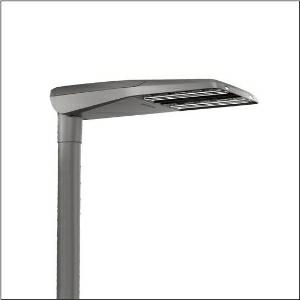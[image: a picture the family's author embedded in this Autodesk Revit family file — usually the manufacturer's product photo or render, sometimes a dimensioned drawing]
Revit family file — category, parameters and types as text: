
# Revit family: streetlight_sl_11_iq_midi___st1_0p1_0_5xc3k51g08me_2a46
name_source: partatom
category: Lighting Fixtures
units: mm (PartAtom-declared; Revit-internal decimal feet)

## family parameters
Cut with Voids When Loaded = No
Host = Face
Light Source = No
Part Type = Normal
Room Calculation Point = No
Round Connector Dimension = Use Diameter
Shared = No

## types (1)
- --- (1 x LED, 17540 lm, 122.7 W, 3000K)
    Apparent Load = 123 VA
    CIE Flux Codes = 32 65 95 100 100
    Color Rendering = 70
    Color Temperature = 3000K
    Default Elevation = 1800 mm
    Description = Streetlight SL 11 iQ midi, mast luminaire, primary light control with 3 zone facetted reflector, of plastic, silver coated, highly specular, primary optical cover: cover, of PMMA, transparent, light distribution: ST1.0P1.0, light emission: direct distribution, primary light characteristic: asymmetric, installation type: post-top, side-entry, lamps: LED, High Power LED, rated values: 17.540lm | 122,7W | 143lm/W (begin service life); end service life: 17.540lm | 130,2W; at 50% lumin. flux: 8.770lm | 56,1W | 156,3lm/W, colour temperature: 3000K, colour rendering: CRI > 70, light colour: 730, light setting 1 begin service life: 100% | 17.540lm | 122,7W | 143lm/W | 3.000K, light setting 1 end service life: 130,2W, further light settings possible, control: Street-Remote, Auto-Match, Temp-Guard, Lumen-Switch, Night-Set, Smart-Wire, Light-Fading, Desk-Remote (wireless, voltage-free reading and setting of iQ features in the workshop via application-optimized NFC function/RFID function), optimised constant luminous flux control (CLO 2.0), pre-setting: linear dimming characteristic, with cable H07RN-F 5x 1.5mm², mains connection: 230..240V, AC, 50/60Hz, connection cable pre-assembled, cable length: 12,5m, luminaire housing, of diecast aluminium, powder-coated, Siteco® metallic grey (DB 702S), please order mast flange separately, inclination adjustable without tools: 0°, 5°, 10°, 15° (post-top) | 0°, -5°, -10°, -15° (side-entry), sealing non-destructively replaceable, multi-level sealing system, length: 780mm, width: 376mm, height: 118mm, mast flange for spigot size: 42mm (side-entry): 5XC10008XM4, 60/48mm (side-entry/post-top): 5XC10108XM2, 76/60mm (side-entry/post-top): 5XC10108XM1, equipment: Power, protection rating (complete): IP66, insulation class (complete): insulation class II (safety insulation), certification: CE, ENEC, ENEC+, VDE, impact resistance: IK10, permissible operating ambient temperature for outdoor applications: -25..+50°C, standard-compliant lighting for roads and squares, Environmental Product Declaration (EPD) tested and certified by an independent institute, packaging unit: 1 piece

Light Distribution: ST1.0P1.0
    Height = 118 mm
    Lamp = 1 x LED
    Lamp Light Flux = 17540 lm
    Lamp Power = 122.7 W
    Lamp count = 1
    Length = 780 mm
    Luminous efficacy = 143 lm/W
    Manufacturer = Siteco
    ModVariant = No
    Model = 5XC3K51G08ME
    Number of Poles = 1
    OnlyDefault = Yes
    Power Factor = 1
    Product Name = Streetlight SL 11 iQ midi | ST1.0P1.0
    Product group = mast luminaire | pylon top
    ProductGroupID = 6100
    Protection Class = Protection class II
    Protection Degree = IP 66
    RLX_Detail_Level = 1
    RLX_Emergency_Light_Flux = 0 lm
    RLX_Emergency_Type = 0
    RLX_Emergency_Type_DB = No
    RlxData = <blob elided: 71037 chars, md5=2de02c39>
    Socket = socket
    Standby Power = 0 W
    System Light Flux = 17540 lm
    System Power = 123 W
    Type Comments = factory setting: luminous flux: 100 % | dim-lin: 254 | 553 mA
    Type Image = l_1005960.jpg
    URL = http://relux.com
    VarID = @adj_006697
    Voltage = 0 V
    Weight = 0.00 kg
    Width = 376 mm

## geometry (parser evidence)
native form markers: Blend x4, Sweep x10
no freeform markers — native parametric forms only
